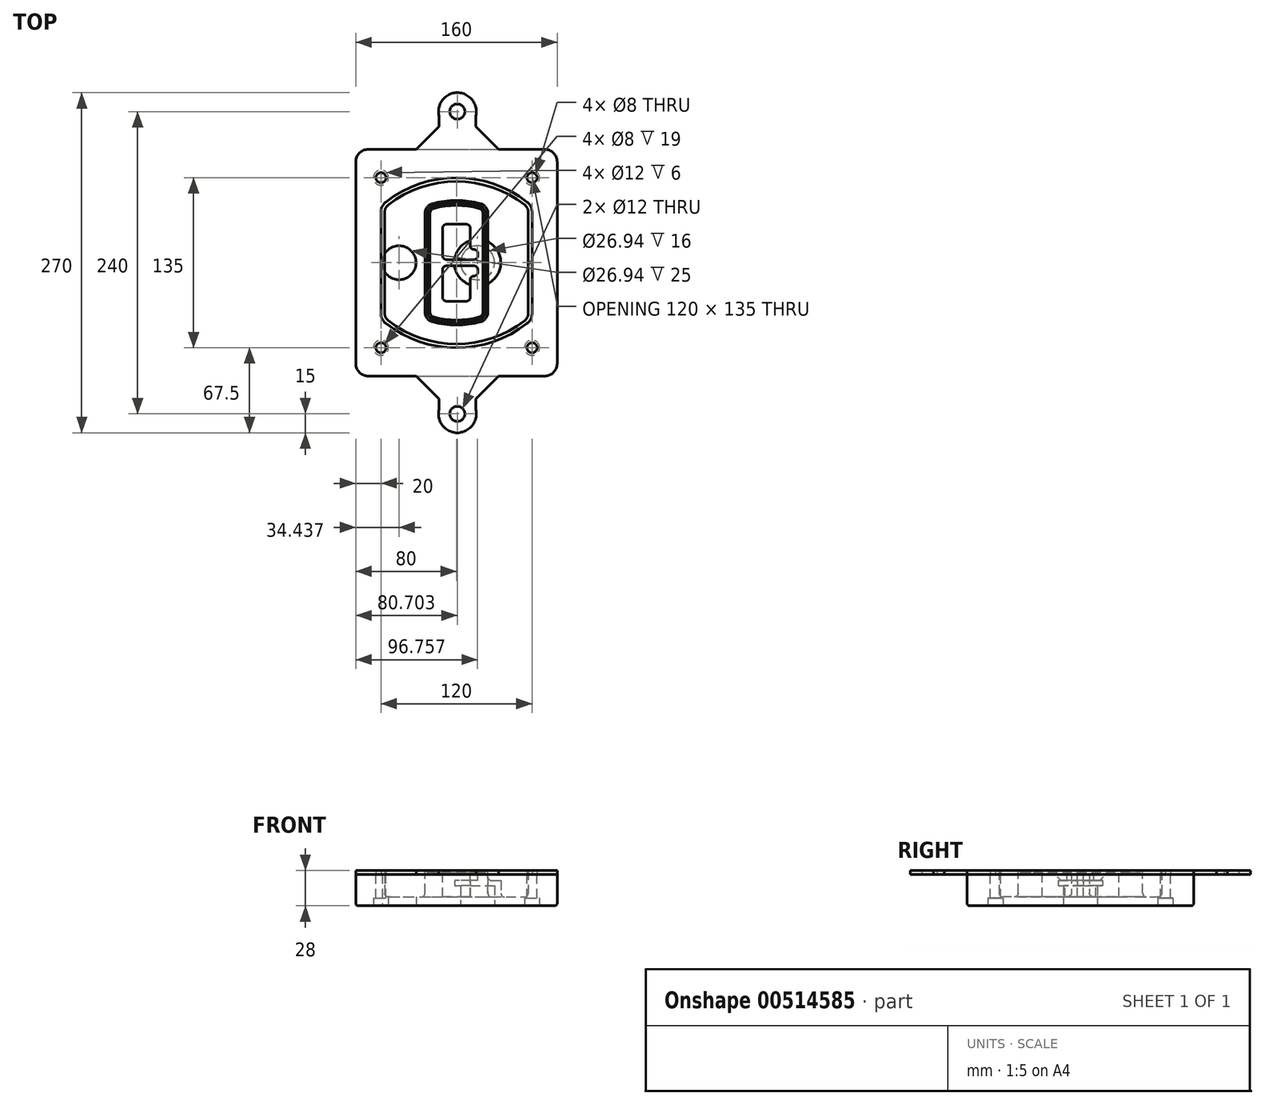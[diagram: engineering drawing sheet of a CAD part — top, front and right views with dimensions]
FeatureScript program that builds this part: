
annotation { "Feature Type Name" : "Feature", "Feature Type Description" : "" }
export const myFeature = defineFeature(function(context is Context, id is Id, definition is map)
    precondition{}
    {
        {
            var Q0;
            Q0=qCreatedBy(makeId("Top.planeOp"),FACE);
            var sketch = newSketch(context, id + "F0", { "sketchPlane" : qUnion([Q0])});
            skPoint(sketch, "E0.rect.middle", {"position": v(0, 0) * mm});
            skLineSegment(sketch, "E1.bottom", {"start": v(-70, -90) * mm, "end": v(70, -90) * mm});
            skLineSegment(sketch, "E1.top", {"start": v(-70, 90) * mm, "end": v(70, 90) * mm});
            skLineSegment(sketch, "E1.left", {"start": v(-80, -80) * mm, "end": v(-80, 80) * mm});
            skLineSegment(sketch, "E1.right", {"start": v(80, -80) * mm, "end": v(80, 80) * mm});
            skLineSegment(sketch, "E2", {"start": v(-80, 90) * mm, "end": v(80, -90) * mm, "construction": true});
            skLineSegment(sketch, "E3", {"start": v(80, 90) * mm, "end": v(-80, -90) * mm, "construction": true});
            skCircle(sketch, "E4", {"center": v(-60, 67.5) * mm, "radius": 4 * mm});
            skCircle(sketch, "E5", {"center": v(60, 67.5) * mm, "radius": 4 * mm});
            skCircle(sketch, "E6", {"center": v(60, -67.5) * mm, "radius": 4 * mm});
            skCircle(sketch, "E7", {"center": v(-60, -67.5) * mm, "radius": 4 * mm});
            skLineSegment(sketch, "E8", {"start": v(-60, 67.5) * mm, "end": v(60, 67.5) * mm, "construction": true});
            skLineSegment(sketch, "E9", {"start": v(60, 67.5) * mm, "end": v(60, -67.5) * mm, "construction": true});
            skLineSegment(sketch, "E10", {"start": v(60, -67.5) * mm, "end": v(-60, -67.5) * mm, "construction": true});
            skLineSegment(sketch, "E11", {"start": v(-60, -67.5) * mm, "end": v(-60, 67.5) * mm, "construction": true});
            skLineSegment(sketch, "E12", {"start": v(-60, 40.3) * mm, "end": v(-60, -40.3) * mm});
            skLineSegment(sketch, "E13", {"start": v(60, 40.3) * mm, "end": v(60, -40.3) * mm});
            skArc(sketch, "E14", {"start": v(56.15, 48.18) * mm, "mid": v(0, 67.5) * mm, "end": v(-56.15, 48.18) * mm});
            skArc(sketch, "E15", {"start": v(-56.15, -48.18) * mm, "mid": v(0, -67.5) * mm, "end": v(56.15, -48.18) * mm});
            skLineSegment(sketch, "E16", {"start": v(-60, 0) * mm, "end": v(60, 0) * mm, "construction": true});
            skPoint(sketch, "E17.visualSharp", {"position": v(-60, -45) * mm});
            skArc(sketch, "E17.filletArc", {"start": v(-60, -40.3) * mm, "mid": v(-58.99, -44.68) * mm, "end": v(-56.15, -48.18) * mm});
            skPoint(sketch, "E18.visualSharp", {"position": v(-60, 45) * mm});
            skArc(sketch, "E18.filletArc", {"start": v(-56.15, 48.18) * mm, "mid": v(-58.99, 44.68) * mm, "end": v(-60, 40.3) * mm});
            skPoint(sketch, "E19.visualSharp", {"position": v(60, 45) * mm});
            skArc(sketch, "E19.filletArc", {"start": v(60, 40.3) * mm, "mid": v(58.99, 44.68) * mm, "end": v(56.15, 48.18) * mm});
            skPoint(sketch, "E20.visualSharp", {"position": v(60, -45) * mm});
            skArc(sketch, "E20.filletArc", {"start": v(56.15, -48.18) * mm, "mid": v(58.99, -44.68) * mm, "end": v(60, -40.3) * mm});
            skPoint(sketch, "E21.visualSharp", {"position": v(-80, 90) * mm});
            skArc(sketch, "E21.filletArc", {"start": v(-70, 90) * mm, "mid": v(-77.07, 87.07) * mm, "end": v(-80, 80) * mm});
            skPoint(sketch, "E22.visualSharp", {"position": v(80, 90) * mm});
            skArc(sketch, "E22.filletArc", {"start": v(80, 80) * mm, "mid": v(77.07, 87.07) * mm, "end": v(70, 90) * mm});
            skPoint(sketch, "E23.visualSharp", {"position": v(80, -90) * mm});
            skArc(sketch, "E23.filletArc", {"start": v(70, -90) * mm, "mid": v(77.07, -87.07) * mm, "end": v(80, -80) * mm});
            skPoint(sketch, "E24.visualSharp", {"position": v(-80, -90) * mm});
            skArc(sketch, "E24.filletArc", {"start": v(-80, -80) * mm, "mid": v(-77.07, -87.07) * mm, "end": v(-70, -90) * mm});
            skArc(sketch, "E25.0", {"start": v(57, 40.3) * mm, "mid": v(56.3, 43.36) * mm, "end": v(54.3, 45.81) * mm});
            skLineSegment(sketch, "E25.1", {"start": v(57, 40.3) * mm, "end": v(57, -40.3) * mm});
            skArc(sketch, "E25.2", {"start": v(54.3, -45.81) * mm, "mid": v(56.3, -43.36) * mm, "end": v(57, -40.3) * mm});
            skArc(sketch, "E25.3", {"start": v(-54.3, -45.81) * mm, "mid": v(0, -64.5) * mm, "end": v(54.3, -45.81) * mm});
            skArc(sketch, "E25.4", {"start": v(-57, -40.3) * mm, "mid": v(-56.3, -43.36) * mm, "end": v(-54.3, -45.81) * mm});
            skArc(sketch, "E25.5", {"start": v(54.3, 45.81) * mm, "mid": v(0, 64.5) * mm, "end": v(-54.3, 45.81) * mm});
            skLineSegment(sketch, "E25.6", {"start": v(-57, 40.3) * mm, "end": v(-57, -40.3) * mm});
            skArc(sketch, "E25.7", {"start": v(-54.3, 45.81) * mm, "mid": v(-56.3, 43.36) * mm, "end": v(-57, 40.3) * mm});
            skArc(sketch, "E26.0", {"start": v(-58.62, 51.33) * mm, "mid": v(-62.58, 46.43) * mm, "end": v(-64, 40.3) * mm});
            skArc(sketch, "E26.1", {"start": v(58.62, 51.33) * mm, "mid": v(0, 71.5) * mm, "end": v(-58.62, 51.33) * mm});
            skArc(sketch, "E26.2", {"start": v(64, 40.3) * mm, "mid": v(62.58, 46.43) * mm, "end": v(58.62, 51.33) * mm});
            skLineSegment(sketch, "E26.3", {"start": v(64, 40.3) * mm, "end": v(64, -40.3) * mm});
            skArc(sketch, "E26.4", {"start": v(58.62, -51.33) * mm, "mid": v(62.58, -46.43) * mm, "end": v(64, -40.3) * mm});
            skLineSegment(sketch, "E26.5", {"start": v(-64, 40.3) * mm, "end": v(-64, -40.3) * mm});
            skArc(sketch, "E26.6", {"start": v(-58.62, -51.33) * mm, "mid": v(0, -71.5) * mm, "end": v(58.62, -51.33) * mm});
            skArc(sketch, "E26.7", {"start": v(-64, -40.3) * mm, "mid": v(-62.58, -46.43) * mm, "end": v(-58.62, -51.33) * mm});
            skSolve(sketch);
        }
        {
            var Q0;
            Q0=makeQuery(id+"F0.imprint","IMPRINT",FACE,{"disambiguationData":[TD([[makeQuery(id+"F0.imprint","IMPRINT",EDGE,{"derivedFrom":sQuery(id+"F0.wireOp",EDGE,"E1.bottom")}),1.0]])]});
            var Q1;
            Q1=makeQuery(id+"F0.imprint","IMPRINT",FACE,{"disambiguationData":[TD([[makeQuery(id+"F0.imprint","IMPRINT",EDGE,{"derivedFrom":sQuery(id+"F0.wireOp",EDGE,"E12")}),1.0]])]});
            var Q2;
            Q2=makeQuery(id+"F0.imprint","IMPRINT",FACE,{"disambiguationData":[TD([[makeQuery(id+"F0.imprint","IMPRINT",EDGE,{"derivedFrom":sQuery(id+"F0.wireOp",EDGE,"E25.0")}),1.0]])]});
            var Q3;
            Q3=makeQuery(id+"F0.imprint","IMPRINT",FACE,{"disambiguationData":[TD([[makeQuery(id+"F0.imprint","IMPRINT",EDGE,{"derivedFrom":sQuery(id+"F0.wireOp",EDGE,"E12")}),-1.0]])]});
            extrude(context, id + "F1", {"entities" : qUnion([Q0, Q1, Q2, Q3]), "oppositeDirection" : true, "depth" : 25 * mm});
        }
        {
            var Q0;
            Q0=makeQuery(id+"F0.imprint","IMPRINT",FACE,{"disambiguationData":[TD([[makeQuery(id+"F0.imprint","IMPRINT",EDGE,{"derivedFrom":sQuery(id+"F0.wireOp",EDGE,"E12")}),1.0]])]});
            extrude(context, id + "F2", {"entities" : qUnion([Q0]), "operationType" : NewBodyOperationType.ADD, "depth" : 3 * mm});
        }
        {
            var Q0;
            Q0=makeQuery(id+"F0.imprint","IMPRINT",FACE,{"disambiguationData":[TD([[makeQuery(id+"F0.imprint","IMPRINT",EDGE,{"derivedFrom":sQuery(id+"F0.wireOp",EDGE,"E25.0")}),1.0]])]});
            extrude(context, id + "F3", {"entities" : qUnion([Q0]), "operationType" : NewBodyOperationType.REMOVE, "oppositeDirection" : true, "depth" : 18 * mm});
        }
        {
            var Q0;
            Q0=makeQuery(id+"F2.opExtrude","CAP_FACE",FACE,{"disambiguationData":[OSD([sQuery(id+"F0.wireOp",EDGE,"E12"),sQuery(id+"F0.wireOp",EDGE,"E13"),sQuery(id+"F0.wireOp",EDGE,"E14"),sQuery(id+"F0.wireOp",EDGE,"E15"),sQuery(id+"F0.wireOp",EDGE,"E17.filletArc"),sQuery(id+"F0.wireOp",EDGE,"E18.filletArc"),sQuery(id+"F0.wireOp",EDGE,"E19.filletArc"),sQuery(id+"F0.wireOp",EDGE,"E20.filletArc"),sQuery(id+"F0.wireOp",EDGE,"E25.0"),sQuery(id+"F0.wireOp",EDGE,"E25.1"),sQuery(id+"F0.wireOp",EDGE,"E25.2"),sQuery(id+"F0.wireOp",EDGE,"E25.3"),sQuery(id+"F0.wireOp",EDGE,"E25.4"),sQuery(id+"F0.wireOp",EDGE,"E25.5"),sQuery(id+"F0.wireOp",EDGE,"E25.6"),sQuery(id+"F0.wireOp",EDGE,"E25.7")])],"isStart":false});
            var sketch = newSketch(context, id + "F4", { "sketchPlane" : qUnion([Q0])});
            skArc(sketch, "E27.0", {"start": v(-19.08, -46.97) * mm, "mid": v(0, -49.5) * mm, "end": v(19.08, -46.97) * mm});
            skArc(sketch, "E28.0", {"start": v(19.08, 46.97) * mm, "mid": v(0, 49.5) * mm, "end": v(-19.08, 46.97) * mm});
            skLineSegment(sketch, "E29", {"start": v(-25, 39.25) * mm, "end": v(-25, -39.25) * mm});
            skLineSegment(sketch, "E30", {"start": v(25, 39.25) * mm, "end": v(25, -39.25) * mm});
            skLineSegment(sketch, "E31", {"start": v(-25, 45.1) * mm, "end": v(25, 45.1) * mm, "construction": true});
            skLineSegment(sketch, "E32", {"start": v(-25, -45.1) * mm, "end": v(25, -45.1) * mm, "construction": true});
            skPoint(sketch, "E33.visualSharp", {"position": v(-25, 45.1) * mm});
            skArc(sketch, "E33.filletArc", {"start": v(-19.08, 46.97) * mm, "mid": v(-23.35, 44.11) * mm, "end": v(-25, 39.25) * mm});
            skPoint(sketch, "E34.visualSharp", {"position": v(25, 45.1) * mm});
            skArc(sketch, "E34.filletArc", {"start": v(25, 39.25) * mm, "mid": v(23.35, 44.11) * mm, "end": v(19.08, 46.97) * mm});
            skPoint(sketch, "E35.visualSharp", {"position": v(25, -45.1) * mm});
            skArc(sketch, "E35.filletArc", {"start": v(19.08, -46.97) * mm, "mid": v(23.35, -44.11) * mm, "end": v(25, -39.25) * mm});
            skPoint(sketch, "E36.visualSharp", {"position": v(-25, -45.1) * mm});
            skArc(sketch, "E36.filletArc", {"start": v(-25, -39.25) * mm, "mid": v(-23.35, -44.11) * mm, "end": v(-19.08, -46.97) * mm});
            skArc(sketch, "E37.0", {"start": v(54.3, 45.81) * mm, "mid": v(0, 64.5) * mm, "end": v(-54.3, 45.81) * mm});
            skArc(sketch, "E37.1", {"start": v(-54.3, 45.81) * mm, "mid": v(-56.3, 43.36) * mm, "end": v(-57, 40.3) * mm});
            skLineSegment(sketch, "E37.2", {"start": v(-57, 40.3) * mm, "end": v(-57, -40.3) * mm});
            skArc(sketch, "E37.3", {"start": v(-57, -40.3) * mm, "mid": v(-56.3, -43.36) * mm, "end": v(-54.3, -45.81) * mm});
            skArc(sketch, "E37.4", {"start": v(-54.3, -45.81) * mm, "mid": v(0, -64.5) * mm, "end": v(54.3, -45.81) * mm});
            skArc(sketch, "E37.5", {"start": v(54.3, -45.81) * mm, "mid": v(56.3, -43.36) * mm, "end": v(57, -40.3) * mm});
            skLineSegment(sketch, "E37.6", {"start": v(57, 40.3) * mm, "end": v(57, -40.3) * mm});
            skArc(sketch, "E37.7", {"start": v(57, 40.3) * mm, "mid": v(56.3, 43.36) * mm, "end": v(54.3, 45.81) * mm});
            skLineSegment(sketch, "E38.0", {"start": v(23, 39.25) * mm, "end": v(23, -39.25) * mm});
            skArc(sketch, "E38.1", {"start": v(18.56, -45.04) * mm, "mid": v(21.76, -42.9) * mm, "end": v(23, -39.25) * mm});
            skArc(sketch, "E38.2", {"start": v(-18.56, -45.04) * mm, "mid": v(0, -47.5) * mm, "end": v(18.56, -45.04) * mm});
            skArc(sketch, "E38.3", {"start": v(-23, -39.25) * mm, "mid": v(-21.76, -42.9) * mm, "end": v(-18.56, -45.04) * mm});
            skLineSegment(sketch, "E38.4", {"start": v(-23, 39.25) * mm, "end": v(-23, -39.25) * mm});
            skArc(sketch, "E38.5", {"start": v(23, 39.25) * mm, "mid": v(21.76, 42.9) * mm, "end": v(18.56, 45.04) * mm});
            skArc(sketch, "E38.6", {"start": v(-18.56, 45.04) * mm, "mid": v(-21.76, 42.9) * mm, "end": v(-23, 39.25) * mm});
            skArc(sketch, "E38.7", {"start": v(18.56, 45.04) * mm, "mid": v(0, 47.5) * mm, "end": v(-18.56, 45.04) * mm});
            skArc(sketch, "E39.0", {"start": v(21, 39.25) * mm, "mid": v(20.18, 41.68) * mm, "end": v(18.04, 43.1) * mm});
            skLineSegment(sketch, "E39.1", {"start": v(21, 39.25) * mm, "end": v(21, -39.25) * mm});
            skArc(sketch, "E39.2", {"start": v(18.04, -43.1) * mm, "mid": v(20.18, -41.68) * mm, "end": v(21, -39.25) * mm});
            skArc(sketch, "E39.3", {"start": v(-18.04, -43.1) * mm, "mid": v(0, -45.5) * mm, "end": v(18.04, -43.1) * mm});
            skArc(sketch, "E39.4", {"start": v(-21, -39.25) * mm, "mid": v(-20.18, -41.68) * mm, "end": v(-18.04, -43.1) * mm});
            skArc(sketch, "E39.5", {"start": v(18.04, 43.1) * mm, "mid": v(0, 45.5) * mm, "end": v(-18.04, 43.1) * mm});
            skLineSegment(sketch, "E39.6", {"start": v(-21, 39.25) * mm, "end": v(-21, -39.25) * mm});
            skArc(sketch, "E39.7", {"start": v(-18.04, 43.1) * mm, "mid": v(-20.18, 41.68) * mm, "end": v(-21, 39.25) * mm});
            skLineSegment(sketch, "E40", {"start": v(-25, 0) * mm, "end": v(25, 0) * mm, "construction": true});
            skLineSegment(sketch, "E41", {"start": v(-11, 5.5) * mm, "end": v(-11, 27.5) * mm});
            skLineSegment(sketch, "E42", {"start": v(-8, 30.5) * mm, "end": v(8, 30.5) * mm});
            skLineSegment(sketch, "E43", {"start": v(11, 27.5) * mm, "end": v(11, 13.5) * mm});
            skLineSegment(sketch, "E44", {"start": v(14, 10.5) * mm, "end": v(14, 10.5) * mm});
            skLineSegment(sketch, "E45", {"start": v(17, 7.5) * mm, "end": v(17, 5.5) * mm});
            skLineSegment(sketch, "E46", {"start": v(14, 2.5) * mm, "end": v(-8, 2.5) * mm});
            skPoint(sketch, "E47.visualSharp", {"position": v(-11, 30.5) * mm});
            skArc(sketch, "E47.filletArc", {"start": v(-8, 30.5) * mm, "mid": v(-10.12, 29.62) * mm, "end": v(-11, 27.5) * mm});
            skPoint(sketch, "E48.visualSharp", {"position": v(11, 30.5) * mm});
            skArc(sketch, "E48.filletArc", {"start": v(11, 27.5) * mm, "mid": v(10.12, 29.62) * mm, "end": v(8, 30.5) * mm});
            skPoint(sketch, "E49.visualSharp", {"position": v(11, 10.5) * mm});
            skArc(sketch, "E49.filletArc", {"start": v(11, 13.5) * mm, "mid": v(11.88, 11.38) * mm, "end": v(14, 10.5) * mm});
            skPoint(sketch, "E50.visualSharp", {"position": v(17, 10.5) * mm});
            skArc(sketch, "E50.filletArc", {"start": v(17, 7.5) * mm, "mid": v(16.12, 9.62) * mm, "end": v(14, 10.5) * mm});
            skPoint(sketch, "E51.visualSharp", {"position": v(17, 2.5) * mm});
            skArc(sketch, "E51.filletArc", {"start": v(14, 2.5) * mm, "mid": v(16.12, 3.38) * mm, "end": v(17, 5.5) * mm});
            skPoint(sketch, "E52.visualSharp", {"position": v(-11, 2.5) * mm});
            skArc(sketch, "E52.filletArc", {"start": v(-11, 5.5) * mm, "mid": v(-10.12, 3.38) * mm, "end": v(-8, 2.5) * mm});
            skLineSegment(sketch, "E53.0.MirrorCS", {"start": v(14, -2.5) * mm, "end": v(-8, -2.5) * mm});
            skArc(sketch, "E54.0.MirrorCS", {"start": v(-11, -5.5) * mm, "mid": v(-10.12, -3.38) * mm, "end": v(-8, -2.5) * mm});
            skLineSegment(sketch, "E55.0.MirrorCS", {"start": v(-11, -5.5) * mm, "end": v(-11, -27.5) * mm});
            skArc(sketch, "E56.0.MirrorCS", {"start": v(-8, -30.5) * mm, "mid": v(-10.12, -29.62) * mm, "end": v(-11, -27.5) * mm});
            skLineSegment(sketch, "E57.0.MirrorCS", {"start": v(-8, -30.5) * mm, "end": v(8, -30.5) * mm});
            skArc(sketch, "E58.0.MirrorCS", {"start": v(11, -27.5) * mm, "mid": v(10.12, -29.62) * mm, "end": v(8, -30.5) * mm});
            skLineSegment(sketch, "E59.0.MirrorCS", {"start": v(11, -27.5) * mm, "end": v(11, -13.5) * mm});
            skArc(sketch, "E60.0.MirrorCS", {"start": v(11, -13.5) * mm, "mid": v(11.88, -11.38) * mm, "end": v(14, -10.5) * mm});
            skArc(sketch, "E61.0.MirrorCS", {"start": v(17, -7.5) * mm, "mid": v(16.12, -9.62) * mm, "end": v(14, -10.5) * mm});
            skLineSegment(sketch, "E62.0.MirrorCS", {"start": v(17, -7.5) * mm, "end": v(17, -5.5) * mm});
            skArc(sketch, "E63.0.MirrorCS", {"start": v(14, -2.5) * mm, "mid": v(16.12, -3.38) * mm, "end": v(17, -5.5) * mm});
            skSolve(sketch);
        }
        {
            var Q0;
            Q0=makeQuery(id+"F4.imprint","IMPRINT",FACE,{"disambiguationData":[TD([[makeQuery(id+"F4.imprint","IMPRINT",EDGE,{"derivedFrom":sQuery(id+"F4.wireOp",EDGE,"E27.0")}),1.0]])]});
            var Q1;
            Q1=makeQuery(id+"F4.imprint","IMPRINT",FACE,{"disambiguationData":[TD([[makeQuery(id+"F4.imprint","IMPRINT",EDGE,{"derivedFrom":sQuery(id+"F4.wireOp",EDGE,"E38.0")}),-1.0]])]});
            var Q2;
            Q2=makeQuery(id+"F4.imprint","IMPRINT",FACE,{"disambiguationData":[TD([[makeQuery(id+"F4.imprint","IMPRINT",EDGE,{"derivedFrom":sQuery(id+"F4.wireOp",EDGE,"E39.0")}),1.0]])]});
            extrude(context, id + "F5", {"entities" : qUnion([Q0, Q1, Q2]), "operationType" : NewBodyOperationType.ADD, "endBound" : BoundingType.UP_TO_NEXT, "oppositeDirection" : true, "depth" : 25 * mm});
        }
        {
            var Q0;
            Q0=makeQuery(id+"F4.imprint","IMPRINT",FACE,{"disambiguationData":[TD([[makeQuery(id+"F4.imprint","IMPRINT",EDGE,{"derivedFrom":sQuery(id+"F4.wireOp",EDGE,"E38.0")}),-1.0]])]});
            extrude(context, id + "F6", {"entities" : qUnion([Q0]), "operationType" : NewBodyOperationType.REMOVE, "oppositeDirection" : true, "depth" : 2 * mm});
        }
        {
            var Q0;
            Q0=makeQuery(id+"F1.opExtrude","CAP_FACE",FACE,{"disambiguationData":[OSD([sQuery(id+"F0.wireOp",EDGE,"E1.bottom"),sQuery(id+"F0.wireOp",EDGE,"E1.top"),sQuery(id+"F0.wireOp",EDGE,"E1.left"),sQuery(id+"F0.wireOp",EDGE,"E1.right"),sQuery(id+"F0.wireOp",EDGE,"E4"),sQuery(id+"F0.wireOp",EDGE,"E5"),sQuery(id+"F0.wireOp",EDGE,"E6"),sQuery(id+"F0.wireOp",EDGE,"E7"),sQuery(id+"F0.wireOp",EDGE,"E21.filletArc"),sQuery(id+"F0.wireOp",EDGE,"E22.filletArc"),sQuery(id+"F0.wireOp",EDGE,"E23.filletArc"),sQuery(id+"F0.wireOp",EDGE,"E24.filletArc")])],"isStart":false});
            var sketch = newSketch(context, id + "F7", { "sketchPlane" : qUnion([Q0])});
            skCircle(sketch, "E64", {"center": v(16.76, 0) * mm, "radius": 13.47 * mm});
            skCircle(sketch, "E65", {"center": v(-45.56, 0) * mm, "radius": 13.47 * mm});
            skLineSegment(sketch, "E66", {"start": v(80, 0) * mm, "end": v(-80, 0) * mm});
            skCircle(sketch, "E67", {"center": v(16.76, 0) * mm, "radius": 18.47 * mm});
            skCircle(sketch, "E68", {"center": v(60, -67.5) * mm, "radius": 6 * mm});
            skCircle(sketch, "E69", {"center": v(-60, -67.5) * mm, "radius": 6 * mm});
            skCircle(sketch, "E70", {"center": v(-60, 67.5) * mm, "radius": 6 * mm});
            skCircle(sketch, "E71", {"center": v(60, 67.5) * mm, "radius": 6 * mm});
            skSolve(sketch);
        }
        {
            var Q0;
            {var subQ1=sQuery(id+"F7.wireOp",EDGE,"E66");var subQ4=sQuery(id+"F7.wireOp",EDGE,"E64");var subQ6=makeQuery(id+"F7.imprint","INTERSECT",VERTEX,{"disambiguationData":[OD(0.0)],"derivedFrom":[subQ4,subQ1]});Q0=makeQuery(id+"F7.imprint","IMPRINT",FACE,{"disambiguationData":[TD([[makeQuery(id+"F7.imprint","IMPRINT",EDGE,{"disambiguationData":[TD([[subQ6,-1.0]])],"derivedFrom":subQ4}),-1.0]])]});}
            var Q1;
            {var subQ0=sQuery(id+"F7.wireOp",EDGE,"E66");var subQ1=sQuery(id+"F7.wireOp",EDGE,"E64");var subQ3=makeQuery(id+"F7.imprint","INTERSECT",VERTEX,{"disambiguationData":[OD(0.0)],"derivedFrom":[subQ1,subQ0]});Q1=makeQuery(id+"F7.imprint","IMPRINT",FACE,{"disambiguationData":[TD([[makeQuery(id+"F7.imprint","IMPRINT",EDGE,{"disambiguationData":[TD([[subQ3,-1.0]])],"derivedFrom":subQ1}),1.0]])]});}
            var Q2;
            {var subQ0=sQuery(id+"F7.wireOp",EDGE,"E66");var subQ1=sQuery(id+"F7.wireOp",EDGE,"E64");var subQ3=makeQuery(id+"F7.imprint","INTERSECT",VERTEX,{"disambiguationData":[OD(0.0)],"derivedFrom":[subQ1,subQ0]});Q2=makeQuery(id+"F7.imprint","IMPRINT",FACE,{"disambiguationData":[TD([[makeQuery(id+"F7.imprint","IMPRINT",EDGE,{"disambiguationData":[TD([[subQ3,1.0]])],"derivedFrom":subQ1}),1.0]])]});}
            var Q3;
            {var subQ1=sQuery(id+"F7.wireOp",EDGE,"E66");var subQ4=sQuery(id+"F7.wireOp",EDGE,"E64");var subQ6=makeQuery(id+"F7.imprint","INTERSECT",VERTEX,{"disambiguationData":[OD(0.0)],"derivedFrom":[subQ4,subQ1]});Q3=makeQuery(id+"F7.imprint","IMPRINT",FACE,{"disambiguationData":[TD([[makeQuery(id+"F7.imprint","IMPRINT",EDGE,{"disambiguationData":[TD([[subQ6,1.0]])],"derivedFrom":subQ4}),-1.0]])]});}
            extrude(context, id + "F8", {"entities" : qUnion([Q0, Q1, Q2, Q3]), "operationType" : NewBodyOperationType.ADD, "oppositeDirection" : true, "depth" : 20 * mm});
        }
        {
            var Q0;
            {var subQ0=sQuery(id+"F7.wireOp",EDGE,"E66");var subQ1=sQuery(id+"F7.wireOp",EDGE,"E64");var subQ3=makeQuery(id+"F7.imprint","INTERSECT",VERTEX,{"disambiguationData":[OD(0.0)],"derivedFrom":[subQ1,subQ0]});Q0=makeQuery(id+"F7.imprint","IMPRINT",FACE,{"disambiguationData":[TD([[makeQuery(id+"F7.imprint","IMPRINT",EDGE,{"disambiguationData":[TD([[subQ3,-1.0]])],"derivedFrom":subQ1}),1.0]])]});}
            var Q1;
            {var subQ0=sQuery(id+"F7.wireOp",EDGE,"E66");var subQ1=sQuery(id+"F7.wireOp",EDGE,"E64");var subQ3=makeQuery(id+"F7.imprint","INTERSECT",VERTEX,{"disambiguationData":[OD(0.0)],"derivedFrom":[subQ1,subQ0]});Q1=makeQuery(id+"F7.imprint","IMPRINT",FACE,{"disambiguationData":[TD([[makeQuery(id+"F7.imprint","IMPRINT",EDGE,{"disambiguationData":[TD([[subQ3,1.0]])],"derivedFrom":subQ1}),1.0]])]});}
            extrude(context, id + "F9", {"entities" : qUnion([Q0, Q1]), "operationType" : NewBodyOperationType.REMOVE, "oppositeDirection" : true, "depth" : 16 * mm});
        }
        {
            var Q0;
            {var subQ0=sQuery(id+"F7.wireOp",EDGE,"E66");var subQ1=sQuery(id+"F7.wireOp",EDGE,"E65");var subQ3=makeQuery(id+"F7.imprint","INTERSECT",VERTEX,{"disambiguationData":[OD(0.0)],"derivedFrom":[subQ1,subQ0]});Q0=makeQuery(id+"F7.imprint","IMPRINT",FACE,{"disambiguationData":[TD([[makeQuery(id+"F7.imprint","IMPRINT",EDGE,{"disambiguationData":[TD([[subQ3,-1.0]])],"derivedFrom":subQ1}),1.0]])]});}
            var Q1;
            {var subQ0=sQuery(id+"F7.wireOp",EDGE,"E66");var subQ1=sQuery(id+"F7.wireOp",EDGE,"E65");var subQ3=makeQuery(id+"F7.imprint","INTERSECT",VERTEX,{"disambiguationData":[OD(0.0)],"derivedFrom":[subQ1,subQ0]});Q1=makeQuery(id+"F7.imprint","IMPRINT",FACE,{"disambiguationData":[TD([[makeQuery(id+"F7.imprint","IMPRINT",EDGE,{"disambiguationData":[TD([[subQ3,1.0]])],"derivedFrom":subQ1}),1.0]])]});}
            extrude(context, id + "F10", {"entities" : qUnion([Q0, Q1]), "operationType" : NewBodyOperationType.REMOVE, "oppositeDirection" : true, "depth" : 25 * mm});
        }
        {
            var Q0;
            Q0=makeQuery(id+"F7.imprint","IMPRINT",FACE,{"disambiguationData":[TD([[makeQuery(id+"F7.imprint","IMPRINT",EDGE,{"derivedFrom":sQuery(id+"F7.wireOp",EDGE,"E68")}),1.0]])]});
            var Q1;
            Q1=makeQuery(id+"F7.imprint","IMPRINT",FACE,{"disambiguationData":[TD([[makeQuery(id+"F7.imprint","IMPRINT",EDGE,{"derivedFrom":makeQuery(id+"F1.opExtrude","CAP_EDGE",EDGE,{"disambiguationData":[OSD([sQuery(id+"F0.wireOp",EDGE,"E5")])],"isStart":false})}),-1.0]])]});
            var Q2;
            Q2=makeQuery(id+"F7.imprint","IMPRINT",FACE,{"disambiguationData":[TD([[makeQuery(id+"F7.imprint","IMPRINT",EDGE,{"derivedFrom":sQuery(id+"F7.wireOp",EDGE,"E69")}),1.0]])]});
            var Q3;
            Q3=makeQuery(id+"F7.imprint","IMPRINT",FACE,{"disambiguationData":[TD([[makeQuery(id+"F7.imprint","IMPRINT",EDGE,{"derivedFrom":makeQuery(id+"F1.opExtrude","CAP_EDGE",EDGE,{"disambiguationData":[OSD([sQuery(id+"F0.wireOp",EDGE,"E4")])],"isStart":false})}),-1.0]])]});
            var Q4;
            Q4=makeQuery(id+"F7.imprint","IMPRINT",FACE,{"disambiguationData":[TD([[makeQuery(id+"F7.imprint","IMPRINT",EDGE,{"derivedFrom":sQuery(id+"F7.wireOp",EDGE,"E70")}),1.0]])]});
            var Q5;
            Q5=makeQuery(id+"F7.imprint","IMPRINT",FACE,{"disambiguationData":[TD([[makeQuery(id+"F7.imprint","IMPRINT",EDGE,{"derivedFrom":makeQuery(id+"F1.opExtrude","CAP_EDGE",EDGE,{"disambiguationData":[OSD([sQuery(id+"F0.wireOp",EDGE,"E7")])],"isStart":false})}),-1.0]])]});
            var Q6;
            Q6=makeQuery(id+"F7.imprint","IMPRINT",FACE,{"disambiguationData":[TD([[makeQuery(id+"F7.imprint","IMPRINT",EDGE,{"derivedFrom":sQuery(id+"F7.wireOp",EDGE,"E71")}),1.0]])]});
            var Q7;
            Q7=makeQuery(id+"F7.imprint","IMPRINT",FACE,{"disambiguationData":[TD([[makeQuery(id+"F7.imprint","IMPRINT",EDGE,{"derivedFrom":makeQuery(id+"F1.opExtrude","CAP_EDGE",EDGE,{"disambiguationData":[OSD([sQuery(id+"F0.wireOp",EDGE,"E6")])],"isStart":false})}),-1.0]])]});
            extrude(context, id + "F11", {"entities" : qUnion([Q0, Q1, Q2, Q3, Q4, Q5, Q6, Q7]), "operationType" : NewBodyOperationType.REMOVE, "oppositeDirection" : true, "depth" : 6 * mm});
        }
        {
            var Q0;
            Q0=makeQuery(id+"F9.boolean.opBoolean","COPY",FACE,{"derivedFrom":makeQuery(id+"F9.opExtrude","CAP_FACE",FACE,{"disambiguationData":[OSD([sQuery(id+"F7.wireOp",EDGE,"E64")])],"isStart":false})});
            var sketch = newSketch(context, id + "F12", { "sketchPlane" : qUnion([Q0])});
            skArc(sketch, "E72.0", {"start": v(11, 17.55) * mm, "mid": v(2.57, 11.82) * mm, "end": v(-1.54, 2.5) * mm});
            skArc(sketch, "E72.1", {"start": v(-1.54, -2.5) * mm, "mid": v(2.57, -11.82) * mm, "end": v(11, -17.55) * mm});
            skLineSegment(sketch, "E73", {"start": v(-1.54, -2.5) * mm, "end": v(14, -2.5) * mm});
            skLineSegment(sketch, "E74.0", {"start": v(14, 2.5) * mm, "end": v(-1.54, 2.5) * mm});
            skArc(sketch, "E74.1", {"start": v(14, 2.5) * mm, "mid": v(16.12, 3.38) * mm, "end": v(17, 5.5) * mm});
            skLineSegment(sketch, "E74.2", {"start": v(17, 7.5) * mm, "end": v(17, 5.5) * mm});
            skArc(sketch, "E74.3", {"start": v(17, 7.5) * mm, "mid": v(16.12, 9.62) * mm, "end": v(14, 10.5) * mm});
            skArc(sketch, "E74.4", {"start": v(11, 13.5) * mm, "mid": v(11.88, 11.38) * mm, "end": v(14, 10.5) * mm});
            skLineSegment(sketch, "E74.5", {"start": v(11, 17.55) * mm, "end": v(11, 13.5) * mm});
            skLineSegment(sketch, "E74.7", {"start": v(14, -2.5) * mm, "end": v(-1.54, -2.5) * mm});
            skArc(sketch, "E74.8", {"start": v(14, -2.5) * mm, "mid": v(16.12, -3.38) * mm, "end": v(17, -5.5) * mm});
            skLineSegment(sketch, "E74.9", {"start": v(17, -7.5) * mm, "end": v(17, -5.5) * mm});
            skArc(sketch, "E74.10", {"start": v(17, -7.5) * mm, "mid": v(16.12, -9.62) * mm, "end": v(14, -10.5) * mm});
            skArc(sketch, "E74.11", {"start": v(11, -13.5) * mm, "mid": v(11.88, -11.38) * mm, "end": v(14, -10.5) * mm});
            skLineSegment(sketch, "E74.12", {"start": v(11, -17.55) * mm, "end": v(11, -13.5) * mm});
            skPoint(sketch, "E75.orphan", {"position": v(11, -27.5) * mm});
            skPoint(sketch, "E76.orphan", {"position": v(-8, -2.5) * mm});
            skPoint(sketch, "E77.orphan", {"position": v(-8, 2.5) * mm});
            skPoint(sketch, "E78.orphan", {"position": v(11, 27.5) * mm});
            skSolve(sketch);
        }
        {
            var Q0;
            {var subQ7=sQuery(id+"F12.wireOp",EDGE,"E72.0");var subQ14=sQuery(id+"F12.wireOp",EDGE,"E72.1");var subQ16=sQuery(id+"F12.wireOp",EDGE,"E74.1");var subQ18=sQuery(id+"F12.wireOp",EDGE,"E74.8");Q0=qUnion([makeQuery(id+"F12.imprint","IMPRINT",FACE,{"disambiguationData":[TD([[makeQuery(id+"F12.imprint","IMPRINT",EDGE,{"derivedFrom":subQ7}),1.0]])]}),makeQuery(id+"F12.imprint","IMPRINT",FACE,{"disambiguationData":[TD([[makeQuery(id+"F12.imprint","IMPRINT",EDGE,{"derivedFrom":subQ14}),1.0]])]}),makeQuery(id+"F12.imprint","IMPRINT",FACE,{"disambiguationData":[TD([[makeQuery(id+"F12.imprint","IMPRINT",EDGE,{"derivedFrom":subQ16}),1.0]])]}),makeQuery(id+"F12.imprint","IMPRINT",FACE,{"disambiguationData":[TD([[makeQuery(id+"F12.imprint","IMPRINT",EDGE,{"derivedFrom":subQ18}),-1.0]])]})]);}
            var Q1;
            Q1=makeQuery(id+"F5.boolean.opBoolean","SPLIT",FACE,{"disambiguationData":[TD([makeQuery(id+"F5.opExtrude","SWEPT_FACE",FACE,{"disambiguationData":[OSD([sQuery(id+"F4.wireOp",EDGE,"E41")])]})])],"derivedFrom":makeQuery(id+"F3.boolean.opBoolean","COPY",FACE,{"derivedFrom":makeQuery(id+"F3.opExtrude","CAP_FACE",FACE,{"disambiguationData":[OSD([sQuery(id+"F0.wireOp",EDGE,"E25.0"),sQuery(id+"F0.wireOp",EDGE,"E25.1"),sQuery(id+"F0.wireOp",EDGE,"E25.2"),sQuery(id+"F0.wireOp",EDGE,"E25.3"),sQuery(id+"F0.wireOp",EDGE,"E25.4"),sQuery(id+"F0.wireOp",EDGE,"E25.5"),sQuery(id+"F0.wireOp",EDGE,"E25.6"),sQuery(id+"F0.wireOp",EDGE,"E25.7")])],"isStart":false})})});
            extrude(context, id + "F13", {"entities" : qUnion([Q0]), "operationType" : NewBodyOperationType.REMOVE, "endBound" : BoundingType.UP_TO_SURFACE, "endBoundEntityFace" : qUnion([Q1]), "depth" : 25 * mm});
        }
        {
            var Q0;
            Q0=makeQuery(id+"F3.boolean.opBoolean","COPY",EDGE,{"derivedFrom":makeQuery(id+"F3.opExtrude","CAP_EDGE",EDGE,{"disambiguationData":[OSD([sQuery(id+"F0.wireOp",EDGE,"E25.6")])],"isStart":false})});
            var Q1;
            Q1=makeQuery(id+"F8.boolean.opBoolean","INTERSECT",EDGE,{"derivedFrom":[makeQuery(id+"F5.opExtrude","SWEPT_FACE",FACE,{"disambiguationData":[OSD([sQuery(id+"F4.wireOp",EDGE,"E30")])]}),makeQuery(id+"F8.opExtrude","CAP_FACE",FACE,{"disambiguationData":[OSD([sQuery(id+"F7.wireOp",EDGE,"E67")])],"isStart":false})]});
            var Q2;
            Q2=makeQuery(id+"F8.boolean.opBoolean","INTERSECT",EDGE,{"disambiguationData":[OD(1.0)],"derivedFrom":[makeQuery(id+"F5.opExtrude","SWEPT_FACE",FACE,{"disambiguationData":[OSD([sQuery(id+"F4.wireOp",EDGE,"E30")])]}),makeQuery(id+"F8.opExtrude","SWEPT_FACE",FACE,{"disambiguationData":[OSD([sQuery(id+"F7.wireOp",EDGE,"E67")])]})]});
            var Q3;
            {var subQ0=sQuery(id+"F4.wireOp",EDGE,"E30");Q3=makeQuery(id+"F8.boolean.opBoolean","SPLIT",EDGE,{"disambiguationData":[TD([makeQuery(id+"F5.opExtrude","SWEPT_FACE",FACE,{"disambiguationData":[OSD([sQuery(id+"F4.wireOp",EDGE,"E35.filletArc")])]})])],"derivedFrom":makeQuery(id+"F5.opExtrude","CAP_EDGE",EDGE,{"disambiguationData":[OSD([subQ0])],"isStart":false})});}
            var Q4;
            {var subQ0=sQuery(id+"F0.wireOp",EDGE,"E25.7");var subQ1=sQuery(id+"F0.wireOp",EDGE,"E25.1");var subQ2=sQuery(id+"F0.wireOp",EDGE,"E25.6");var subQ3=sQuery(id+"F0.wireOp",EDGE,"E25.5");var subQ4=sQuery(id+"F0.wireOp",EDGE,"E25.4");var subQ5=sQuery(id+"F0.wireOp",EDGE,"E25.0");var subQ6=sQuery(id+"F0.wireOp",EDGE,"E25.2");var subQ7=sQuery(id+"F0.wireOp",EDGE,"E25.3");Q4=makeQuery(id+"F8.boolean.opBoolean","INTERSECT",EDGE,{"derivedFrom":[makeQuery(id+"F5.boolean.opBoolean","SPLIT",FACE,{"disambiguationData":[TD([makeQuery(id+"F2.opExtrude","SWEPT_FACE",FACE,{"disambiguationData":[OSD([subQ5])]})])],"derivedFrom":makeQuery(id+"F3.boolean.opBoolean","COPY",FACE,{"derivedFrom":makeQuery(id+"F3.opExtrude","CAP_FACE",FACE,{"disambiguationData":[OSD([subQ5,subQ1,subQ6,subQ7,subQ4,subQ3,subQ2,subQ0])],"isStart":false})})}),makeQuery(id+"F8.opExtrude","SWEPT_FACE",FACE,{"disambiguationData":[OSD([sQuery(id+"F7.wireOp",EDGE,"E67")])]})]});}
            var Q5;
            Q5=makeQuery(id+"F8.boolean.opBoolean","INTERSECT",EDGE,{"disambiguationData":[OD(0.0)],"derivedFrom":[makeQuery(id+"F5.opExtrude","SWEPT_FACE",FACE,{"disambiguationData":[OSD([sQuery(id+"F4.wireOp",EDGE,"E30")])]}),makeQuery(id+"F8.opExtrude","SWEPT_FACE",FACE,{"disambiguationData":[OSD([sQuery(id+"F7.wireOp",EDGE,"E67")])]})]});
            fillet(context, id + "F14", {"entities" : qUnion([Q0, Q1, Q2, Q3, Q4, Q5]), "radius" : 3 * mm, "tangentPropagation" : true, "allowEdgeOverflow" : false});
        }
        {
            var Q0;
            Q0=makeQuery(id+"F1.opExtrude","CAP_EDGE",EDGE,{"disambiguationData":[OSD([sQuery(id+"F0.wireOp",EDGE,"E1.bottom")])],"isStart":false});
            fillet(context, id + "F15", {"entities" : qUnion([Q0]), "radius" : 2 * mm, "tangentPropagation" : true, "allowEdgeOverflow" : false});
        }
        {
            var Q0;
            {var subQ0=sQuery(id+"F0.wireOp",EDGE,"E21.filletArc");var subQ1=sQuery(id+"F0.wireOp",EDGE,"E7");var subQ2=sQuery(id+"F0.wireOp",EDGE,"E6");var subQ3=sQuery(id+"F0.wireOp",EDGE,"E5");var subQ4=sQuery(id+"F0.wireOp",EDGE,"E4");var subQ5=sQuery(id+"F0.wireOp",EDGE,"E22.filletArc");var subQ6=sQuery(id+"F0.wireOp",EDGE,"E1.bottom");var subQ7=sQuery(id+"F0.wireOp",EDGE,"E1.right");var subQ8=sQuery(id+"F0.wireOp",EDGE,"E1.top");var subQ9=sQuery(id+"F0.wireOp",EDGE,"E1.left");var subQ10=sQuery(id+"F0.wireOp",EDGE,"E23.filletArc");var subQ11=sQuery(id+"F0.wireOp",EDGE,"E24.filletArc");Q0=makeQuery(id+"F2.boolean.opBoolean","SPLIT",FACE,{"disambiguationData":[TD([makeQuery(id+"F1.opExtrude","SWEPT_FACE",FACE,{"disambiguationData":[OSD([subQ6])]})])],"derivedFrom":makeQuery(id+"F1.opExtrude","CAP_FACE",FACE,{"disambiguationData":[OSD([subQ6,subQ8,subQ9,subQ7,subQ4,subQ3,subQ2,subQ1,subQ0,subQ5,subQ10,subQ11])],"isStart":true})});}
            var sketch = newSketch(context, id + "F16", { "sketchPlane" : qUnion([Q0])});
            skArc(sketch, "E79.0", {"start": v(56.15, 48.18) * mm, "mid": v(0, 67.5) * mm, "end": v(-56.15, 48.18) * mm});
            skArc(sketch, "E79.1", {"start": v(-56.15, 48.18) * mm, "mid": v(-58.99, 44.68) * mm, "end": v(-60, 40.3) * mm});
            skLineSegment(sketch, "E79.2", {"start": v(-60, 40.3) * mm, "end": v(-60, -40.3) * mm});
            skArc(sketch, "E79.3", {"start": v(-60, -40.3) * mm, "mid": v(-58.99, -44.68) * mm, "end": v(-56.15, -48.18) * mm});
            skArc(sketch, "E79.4", {"start": v(-56.15, -48.18) * mm, "mid": v(0, -67.5) * mm, "end": v(56.15, -48.18) * mm});
            skCircle(sketch, "E79.5", {"center": v(-60, 67.5) * mm, "radius": 4 * mm});
            skCircle(sketch, "E79.6", {"center": v(60, 67.5) * mm, "radius": 4 * mm});
            skLineSegment(sketch, "E79.7", {"start": v(-80, -80) * mm, "end": v(-80, 80) * mm});
            skCircle(sketch, "E79.8", {"center": v(-60, -67.5) * mm, "radius": 4 * mm});
            skCircle(sketch, "E79.9", {"center": v(60, -67.5) * mm, "radius": 4 * mm});
            skLineSegment(sketch, "E79.10", {"start": v(60, 40.3) * mm, "end": v(60, -40.3) * mm});
            skArc(sketch, "E79.11", {"start": v(56.15, -48.18) * mm, "mid": v(58.99, -44.68) * mm, "end": v(60, -40.3) * mm});
            skArc(sketch, "E79.12", {"start": v(60, 40.3) * mm, "mid": v(58.99, 44.68) * mm, "end": v(56.15, 48.18) * mm});
            skLineSegment(sketch, "E79.13", {"start": v(80, -80) * mm, "end": v(80, 80) * mm});
            skArc(sketch, "E79.14", {"start": v(80, 80) * mm, "mid": v(77.07, 87.07) * mm, "end": v(70, 90) * mm});
            skArc(sketch, "E79.15", {"start": v(-70, 90) * mm, "mid": v(-77.07, 87.07) * mm, "end": v(-80, 80) * mm});
            skLineSegment(sketch, "E79.16", {"start": v(-70, 90) * mm, "end": v(70, 90) * mm});
            skArc(sketch, "E79.17", {"start": v(70, -90) * mm, "mid": v(77.07, -87.07) * mm, "end": v(80, -80) * mm});
            skLineSegment(sketch, "E79.18", {"start": v(-70, -90) * mm, "end": v(70, -90) * mm});
            skArc(sketch, "E79.19", {"start": v(-80, -80) * mm, "mid": v(-77.07, -87.07) * mm, "end": v(-70, -90) * mm});
            skLineSegment(sketch, "E80", {"start": v(-31.91, 90) * mm, "end": v(-13.91, 108) * mm});
            skLineSegment(sketch, "E81", {"start": v(-13.91, 108) * mm, "end": v(-13.91, 116.63) * mm});
            skLineSegment(sketch, "E82", {"start": v(15.32, 108) * mm, "end": v(33.32, 90) * mm});
            skLineSegment(sketch, "E83", {"start": v(15.32, 116.63) * mm, "end": v(15.32, 108) * mm});
            skArc(sketch, "E84", {"start": v(15.32, 116.63) * mm, "mid": v(0.7, 135) * mm, "end": v(-13.91, 116.63) * mm});
            skCircle(sketch, "E85", {"center": v(0.7, 120) * mm, "radius": 6 * mm});
            skLineSegment(sketch, "E86", {"start": v(0.7, 120) * mm, "end": v(0.7, 90) * mm, "construction": true});
            skLineSegment(sketch, "E87", {"start": v(-80, 0) * mm, "end": v(80, 0) * mm, "construction": true});
            skLineSegment(sketch, "E88.MirrorCS", {"start": v(-13.91, 108) * mm, "end": v(-31.91, 90) * mm});
            skLineSegment(sketch, "E89.MirrorCS", {"start": v(33.32, 90) * mm, "end": v(15.32, 108) * mm});
            skLineSegment(sketch, "E90.MirrorCS", {"start": v(-13.91, 116.63) * mm, "end": v(-13.91, 108) * mm});
            skLineSegment(sketch, "E91.MirrorCS", {"start": v(15.32, 108) * mm, "end": v(15.32, 116.63) * mm});
            skArc(sketch, "E92.MirrorCS", {"start": v(-13.91, 116.63) * mm, "mid": v(0.7, 135) * mm, "end": v(15.32, 116.63) * mm});
            skLineSegment(sketch, "E93.MirrorCS", {"start": v(0.7, -120) * mm, "end": v(0.7, -90) * mm, "construction": true});
            skLineSegment(sketch, "E94.MirrorCS", {"start": v(15.32, -108) * mm, "end": v(33.32, -90) * mm});
            skLineSegment(sketch, "E95.MirrorCS", {"start": v(15.32, -108) * mm, "end": v(15.32, -116.63) * mm});
            skCircle(sketch, "E96.MirrorC", {"center": v(0.7, -120) * mm, "radius": 6 * mm});
            skArc(sketch, "E97.MirrorCS", {"start": v(15.32, -116.63) * mm, "mid": v(0.7, -135) * mm, "end": v(-13.91, -116.63) * mm});
            skLineSegment(sketch, "E98.MirrorCS", {"start": v(-13.91, -108) * mm, "end": v(-13.91, -116.63) * mm});
            skLineSegment(sketch, "E99.MirrorCS", {"start": v(-13.91, -108) * mm, "end": v(-31.91, -90) * mm});
            skSolve(sketch);
        }
        {
            var Q0;
            Q0 = qSketchRegion(id + "F16", true);
            var Q1;
            Q1=makeQuery(id+"F2.opExtrude","CAP_FACE",FACE,{"disambiguationData":[OSD([sQuery(id+"F0.wireOp",EDGE,"E12"),sQuery(id+"F0.wireOp",EDGE,"E13"),sQuery(id+"F0.wireOp",EDGE,"E14"),sQuery(id+"F0.wireOp",EDGE,"E15"),sQuery(id+"F0.wireOp",EDGE,"E17.filletArc"),sQuery(id+"F0.wireOp",EDGE,"E18.filletArc"),sQuery(id+"F0.wireOp",EDGE,"E19.filletArc"),sQuery(id+"F0.wireOp",EDGE,"E20.filletArc"),sQuery(id+"F0.wireOp",EDGE,"E25.0"),sQuery(id+"F0.wireOp",EDGE,"E25.1"),sQuery(id+"F0.wireOp",EDGE,"E25.2"),sQuery(id+"F0.wireOp",EDGE,"E25.3"),sQuery(id+"F0.wireOp",EDGE,"E25.4"),sQuery(id+"F0.wireOp",EDGE,"E25.5"),sQuery(id+"F0.wireOp",EDGE,"E25.6"),sQuery(id+"F0.wireOp",EDGE,"E25.7")])],"isStart":false});
            extrude(context, id + "F17", {"entities" : qUnion([Q0]), "endBound" : BoundingType.UP_TO_SURFACE, "endBoundEntityFace" : qUnion([Q1]), "depth" : 25 * mm});
        }
    });
